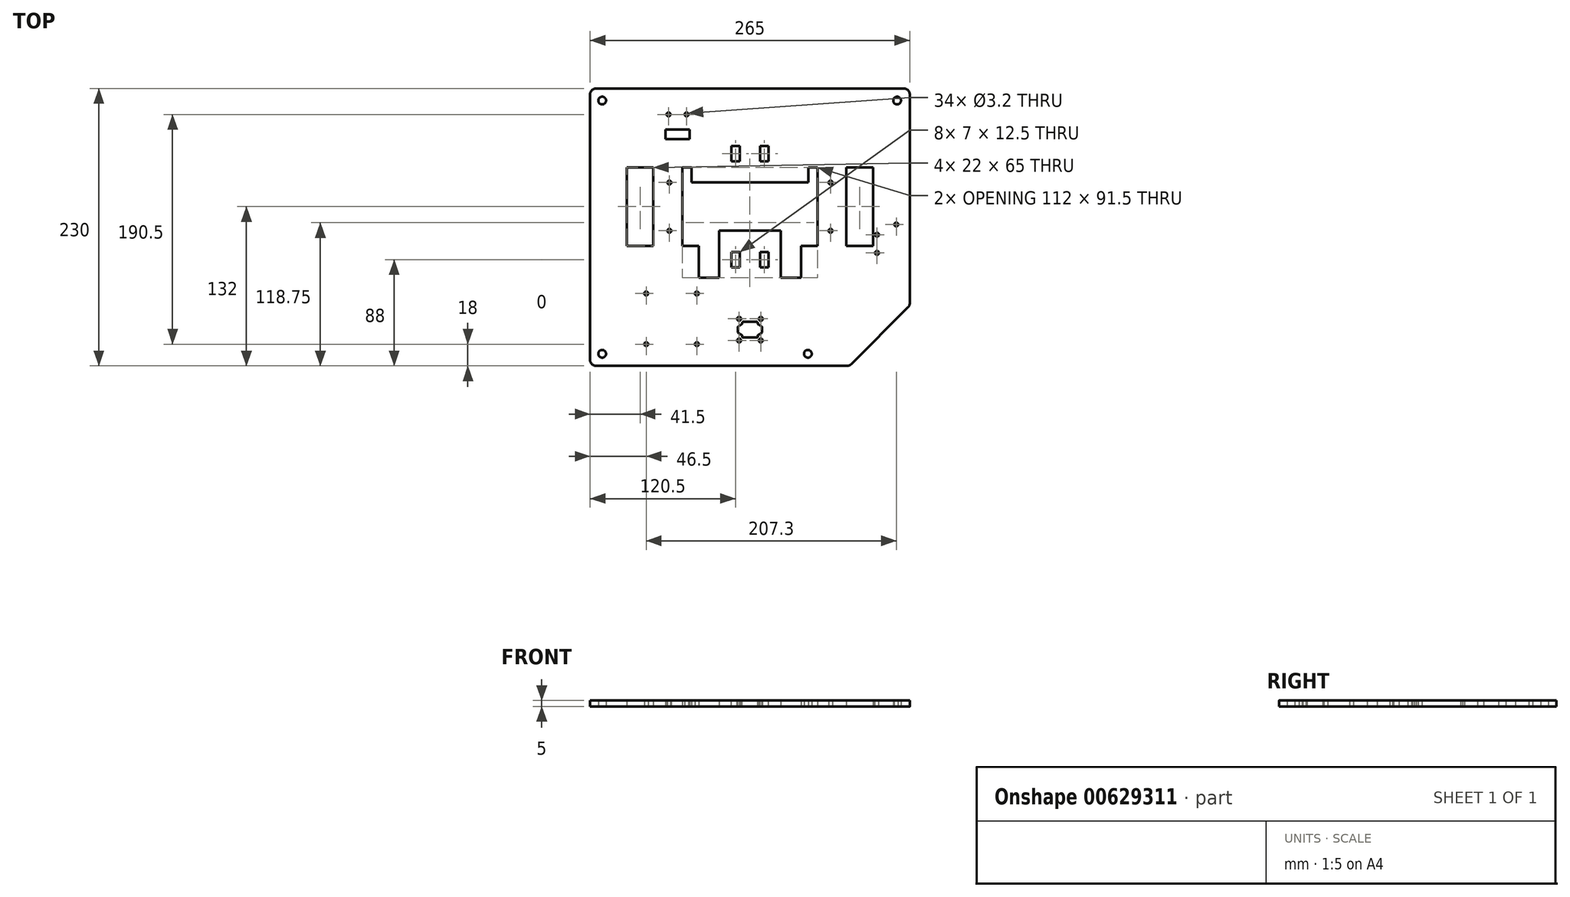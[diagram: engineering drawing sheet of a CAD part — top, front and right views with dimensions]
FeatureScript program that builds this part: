
annotation { "Feature Type Name" : "Feature", "Feature Type Description" : "" }
export const myFeature = defineFeature(function(context is Context, id is Id, definition is map)
    precondition{}
    {
        {
            var Q0;
            Q0=qCreatedBy(makeId("Top.planeOp"),FACE);
            var sketch = newSketch(context, id + "F0", { "sketchPlane" : qUnion([Q0])});
            skLineSegment(sketch, "E0.bottom", {"start": v(132.5, -132) * mm, "end": v(-132.5, -132) * mm});
            skLineSegment(sketch, "E0.top", {"start": v(132.5, 98) * mm, "end": v(-132.5, 98) * mm});
            skLineSegment(sketch, "E0.left", {"start": v(132.5, -132) * mm, "end": v(132.5, 98) * mm});
            skLineSegment(sketch, "E0.right", {"start": v(-132.5, -132) * mm, "end": v(-132.5, 98) * mm});
            skPoint(sketch, "E0.middle", {"position": v(0, -17) * mm});
            skLineSegment(sketch, "E1.bottom", {"start": v(-80, -32.5) * mm, "end": v(-102, -32.5) * mm});
            skLineSegment(sketch, "E1.top", {"start": v(-80, 32.5) * mm, "end": v(-102, 32.5) * mm});
            skLineSegment(sketch, "E1.left", {"start": v(-80, -32.5) * mm, "end": v(-80, 32.5) * mm});
            skLineSegment(sketch, "E1.right", {"start": v(-102, -32.5) * mm, "end": v(-102, 32.5) * mm});
            skPoint(sketch, "E1.middle", {"position": v(-91, 0) * mm});
            skLineSegment(sketch, "E2.bottom", {"start": v(102, -32.5) * mm, "end": v(80, -32.5) * mm});
            skLineSegment(sketch, "E2.top", {"start": v(102, 32.5) * mm, "end": v(80, 32.5) * mm});
            skLineSegment(sketch, "E2.left", {"start": v(102, -32.5) * mm, "end": v(102, 32.5) * mm});
            skLineSegment(sketch, "E2.right", {"start": v(80, -32.5) * mm, "end": v(80, 32.5) * mm});
            skPoint(sketch, "E2.middle", {"position": v(91, 0) * mm});
            skLineSegment(sketch, "E3.bottom", {"start": v(56, -32.5) * mm, "end": v(42.5, -32.5) * mm});
            skLineSegment(sketch, "E3.top", {"start": v(56, 32.5) * mm, "end": v(48.5, 32.5) * mm});
            skLineSegment(sketch, "E3.left", {"start": v(56, -32.5) * mm, "end": v(56, 32.5) * mm});
            skLineSegment(sketch, "E3.right", {"start": v(-56, -32.5) * mm, "end": v(-56, 32.5) * mm});
            skPoint(sketch, "E3.middle", {"position": v(0, 0) * mm});
            skPoint(sketch, "E3.middle.positionSnap0", {"position": v(0, 98) * mm});
            skPoint(sketch, "E3.centerSnap0", {"position": v(0, 98) * mm});
            skLineSegment(sketch, "E4.bottom", {"start": v(66.75, -20) * mm, "end": v(-66.75, -20) * mm, "construction": true});
            skLineSegment(sketch, "E4.top", {"start": v(66.75, 20) * mm, "end": v(-66.75, 20) * mm, "construction": true});
            skLineSegment(sketch, "E4.left", {"start": v(66.75, -20) * mm, "end": v(66.75, 20) * mm, "construction": true});
            skLineSegment(sketch, "E4.right", {"start": v(-66.75, -20) * mm, "end": v(-66.75, 20) * mm, "construction": true});
            skLineSegment(sketch, "E5.bottom", {"start": v(-25.5, -59) * mm, "end": v(-42.5, -59) * mm});
            skLineSegment(sketch, "E5.left", {"start": v(-25.5, -59) * mm, "end": v(-25.5, -20) * mm});
            skLineSegment(sketch, "E5.right", {"start": v(-42.5, -59) * mm, "end": v(-42.5, -32.5) * mm});
            skPoint(sketch, "E5.middle", {"position": v(-34, -45.75) * mm});
            skLineSegment(sketch, "E6.bottom", {"start": v(42.5, -59) * mm, "end": v(25.5, -59) * mm});
            skLineSegment(sketch, "E6.left", {"start": v(42.5, -59) * mm, "end": v(42.5, -32.5) * mm});
            skLineSegment(sketch, "E6.right", {"start": v(25.5, -59) * mm, "end": v(25.5, -20) * mm});
            skPoint(sketch, "E6.middle", {"position": v(34, -45.75) * mm});
            skLineSegment(sketch, "E7.trimOffspring", {"start": v(-42.5, -32.5) * mm, "end": v(-56, -32.5) * mm});
            skLineSegment(sketch, "E8.trimOffspring", {"start": v(25.5, -20) * mm, "end": v(-25.5, -20) * mm});
            skLineSegment(sketch, "E9.top", {"start": v(-48.5, 20) * mm, "end": v(48.5, 20) * mm});
            skLineSegment(sketch, "E9.left", {"start": v(-48.5, 32.5) * mm, "end": v(-48.5, 20) * mm});
            skLineSegment(sketch, "E9.right", {"start": v(48.5, 32.5) * mm, "end": v(48.5, 20) * mm});
            skLineSegment(sketch, "E10.trimOffspring", {"start": v(-48.5, 32.5) * mm, "end": v(-56, 32.5) * mm});
            skLineSegment(sketch, "E11", {"start": v(-132.5, 0) * mm, "end": v(132.5, 0) * mm, "construction": true});
            skSolve(sketch);
        }
        {
            var Q0;
            Q0=makeQuery(id+"F0.imprint","IMPRINT",FACE,{"disambiguationData":[TD([[makeQuery(id+"F0.imprint","IMPRINT",EDGE,{"derivedFrom":sQuery(id+"F0.wireOp",EDGE,"E0.bottom")}),-1.0]])]});
            extrude(context, id + "F1", {"entities" : qUnion([Q0]), "depth" : 5 * mm, "offsetDistance" : 25 * mm});
        }
        {
            var Q0;
            Q0=sQuery(id+"F0.wireOp",VERTEX,"E4.right.end");
            var Q1;
            Q1=sQuery(id+"F0.wireOp",VERTEX,"E4.right.start");
            var Q2;
            Q2=sQuery(id+"F0.wireOp",VERTEX,"E4.top.start");
            var Q3;
            Q3=sQuery(id+"F0.wireOp",VERTEX,"E4.bottom.start");
            var Q4;
            Q4=makeQuery(id+"F1.opExtrude","SWEPT_BODY",BODY,{"disambiguationData":[OSD([sQuery(id+"F0.wireOp",EDGE,"E0.bottom"),sQuery(id+"F0.wireOp",EDGE,"E0.top"),sQuery(id+"F0.wireOp",EDGE,"E0.left"),sQuery(id+"F0.wireOp",EDGE,"E0.right"),sQuery(id+"F0.wireOp",EDGE,"E1.bottom"),sQuery(id+"F0.wireOp",EDGE,"E1.top"),sQuery(id+"F0.wireOp",EDGE,"E1.left"),sQuery(id+"F0.wireOp",EDGE,"E1.right"),sQuery(id+"F0.wireOp",EDGE,"E2.bottom"),sQuery(id+"F0.wireOp",EDGE,"E2.top"),sQuery(id+"F0.wireOp",EDGE,"E2.left"),sQuery(id+"F0.wireOp",EDGE,"E2.right"),sQuery(id+"F0.wireOp",EDGE,"E3.bottom"),sQuery(id+"F0.wireOp",EDGE,"E3.top"),sQuery(id+"F0.wireOp",EDGE,"E3.left"),sQuery(id+"F0.wireOp",EDGE,"E3.right")])]});
            hole(context, id + "F2", {"style" : HoleStyle.SIMPLE, "endStyle" : HoleEndStyle.THROUGH, "oppositeDirection" : true, "holeDiameter" : 3.2 * mm, "majorDiameter" : 5 * mm, "isTappedThrough" : true, "tappedDepth" : 2.3 * mm, "tapClearance" : 3, "startFromSketch" : true, "locations" : qUnion([Q0, Q1, Q2, Q3]), "scope" : qUnion([Q4])});
        }
        {
            var Q0;
            Q0=makeQuery(id+"F1.opExtrude","SWEPT_FACE",FACE,{"disambiguationData":[OSD([sQuery(id+"F0.wireOp",EDGE,"E0.bottom")])]});
            var Q1;
            Q1=makeQuery(id+"F1.opExtrude","SWEPT_FACE",FACE,{"disambiguationData":[OSD([sQuery(id+"F0.wireOp",EDGE,"E0.top")])]});
            cPlane(context, id + "F3", {"entities" : qUnion([Q0, Q1]), "cplaneType" : CPlaneType.MID_PLANE, "offset" : 25 * mm, "width" : 150 * mm, "height" : 150 * mm});
        }
        {
            var Q0;
            Q0=makeQuery(id+"F1.opExtrude","CAP_FACE",FACE,{"disambiguationData":[OSD([sQuery(id+"F0.wireOp",EDGE,"E0.bottom"),sQuery(id+"F0.wireOp",EDGE,"E0.top"),sQuery(id+"F0.wireOp",EDGE,"E0.left"),sQuery(id+"F0.wireOp",EDGE,"E0.right"),sQuery(id+"F0.wireOp",EDGE,"E1.bottom"),sQuery(id+"F0.wireOp",EDGE,"E1.top"),sQuery(id+"F0.wireOp",EDGE,"E1.left"),sQuery(id+"F0.wireOp",EDGE,"E1.right"),sQuery(id+"F0.wireOp",EDGE,"E2.bottom"),sQuery(id+"F0.wireOp",EDGE,"E2.top"),sQuery(id+"F0.wireOp",EDGE,"E2.left"),sQuery(id+"F0.wireOp",EDGE,"E2.right"),sQuery(id+"F0.wireOp",EDGE,"E3.bottom"),sQuery(id+"F0.wireOp",EDGE,"E3.top"),sQuery(id+"F0.wireOp",EDGE,"E3.left"),sQuery(id+"F0.wireOp",EDGE,"E3.right")])],"isStart":false});
            var sketch = newSketch(context, id + "F4", { "sketchPlane" : qUnion([Q0])});
            skLineSegment(sketch, "E12", {"start": v(-6.73, -102) * mm, "end": v(6.73, -102) * mm, "construction": true});
            skLineSegment(sketch, "E13.bottom", {"start": v(6.5, -108.5) * mm, "end": v(-6.5, -108.5) * mm});
            skLineSegment(sketch, "E13.top", {"start": v(6.5, -95.5) * mm, "end": v(-6.5, -95.5) * mm});
            skLineSegment(sketch, "E13.left", {"start": v(6.5, -108.5) * mm, "end": v(6.5, -106.52) * mm});
            skLineSegment(sketch, "E13.right", {"start": v(-6.5, -108.5) * mm, "end": v(-6.5, -106.52) * mm});
            skPoint(sketch, "E13.middle", {"position": v(0, -102) * mm});
            skLineSegment(sketch, "E14.bottom", {"start": v(9, -111) * mm, "end": v(-9, -111) * mm, "construction": true});
            skLineSegment(sketch, "E14.top", {"start": v(9, -93) * mm, "end": v(-9, -93) * mm, "construction": true});
            skLineSegment(sketch, "E14.left", {"start": v(9, -111) * mm, "end": v(9, -93) * mm, "construction": true});
            skLineSegment(sketch, "E14.right", {"start": v(-9, -111) * mm, "end": v(-9, -93) * mm, "construction": true});
            skLineSegment(sketch, "E15.left", {"start": v(10, -104.5) * mm, "end": v(10, -99.5) * mm});
            skLineSegment(sketch, "E15.right", {"start": v(-10, -104.5) * mm, "end": v(-10, -99.5) * mm});
            skLineSegment(sketch, "E16.trimOffspring", {"start": v(-6.5, -97.48) * mm, "end": v(-6.5, -95.5) * mm});
            skLineSegment(sketch, "E17.trimOffspring", {"start": v(6.5, -97.48) * mm, "end": v(6.5, -95.5) * mm});
            skLineSegment(sketch, "E18", {"start": v(-10, -99.5) * mm, "end": v(-6.5, -97.48) * mm});
            skLineSegment(sketch, "E19", {"start": v(-10, -104.5) * mm, "end": v(-6.5, -106.52) * mm});
            skLineSegment(sketch, "E20", {"start": v(6.5, -97.48) * mm, "end": v(10, -99.5) * mm});
            skLineSegment(sketch, "E21", {"start": v(10, -104.5) * mm, "end": v(6.5, -106.52) * mm});
            skLineSegment(sketch, "E22", {"start": v(-132.5, -17) * mm, "end": v(132.5, -17) * mm, "construction": true});
            skSolve(sketch);
        }
        {
            var Q0;
            Q0=makeQuery(id+"F4.imprint","IMPRINT",FACE,{"disambiguationData":[TD([[makeQuery(id+"F4.imprint","IMPRINT",EDGE,{"derivedFrom":sQuery(id+"F4.wireOp",EDGE,"E13.bottom")}),-1.0]])]});
            extrude(context, id + "F5", {"entities" : qUnion([Q0]), "operationType" : NewBodyOperationType.REMOVE, "endBound" : BoundingType.UP_TO_NEXT, "oppositeDirection" : true, "depth" : 25 * mm, "offsetDistance" : 25 * mm});
        }
        {
            var Q0;
            Q0=sQuery(id+"F4.wireOp",VERTEX,"E14.top.end");
            var Q1;
            Q1=sQuery(id+"F4.wireOp",VERTEX,"E14.bottom.end");
            var Q2;
            Q2=sQuery(id+"F4.wireOp",VERTEX,"E14.left.end");
            var Q3;
            Q3=sQuery(id+"F4.wireOp",VERTEX,"E14.left.start");
            var Q4;
            Q4=makeQuery(id+"F1.opExtrude","SWEPT_BODY",BODY,{"disambiguationData":[OSD([sQuery(id+"F0.wireOp",EDGE,"E0.bottom"),sQuery(id+"F0.wireOp",EDGE,"E0.top"),sQuery(id+"F0.wireOp",EDGE,"E0.left"),sQuery(id+"F0.wireOp",EDGE,"E0.right"),sQuery(id+"F0.wireOp",EDGE,"E1.bottom"),sQuery(id+"F0.wireOp",EDGE,"E1.top"),sQuery(id+"F0.wireOp",EDGE,"E1.left"),sQuery(id+"F0.wireOp",EDGE,"E1.right"),sQuery(id+"F0.wireOp",EDGE,"E2.bottom"),sQuery(id+"F0.wireOp",EDGE,"E2.top"),sQuery(id+"F0.wireOp",EDGE,"E2.left"),sQuery(id+"F0.wireOp",EDGE,"E2.right"),sQuery(id+"F0.wireOp",EDGE,"E3.bottom"),sQuery(id+"F0.wireOp",EDGE,"E3.top"),sQuery(id+"F0.wireOp",EDGE,"E3.left"),sQuery(id+"F0.wireOp",EDGE,"E3.right")])]});
            hole(context, id + "F6", {"style" : HoleStyle.SIMPLE, "endStyle" : HoleEndStyle.THROUGH, "holeDiameter" : 3.2 * mm, "majorDiameter" : 5 * mm, "isTappedThrough" : true, "tappedDepth" : 2.3 * mm, "tapClearance" : 3, "startFromSketch" : true, "locations" : qUnion([Q0, Q1, Q2, Q3]), "scope" : qUnion([Q4])});
        }
        {
            var Q0;
            Q0=makeQuery(id+"F5.boolean.opBoolean","COPY",EDGE,{"derivedFrom":makeQuery(id+"F5.opExtrude","SWEPT_EDGE",EDGE,{"disambiguationData":[OSD([sQuery(id+"F4.wireOp",EDGE,"E15.right"),sQuery(id+"F4.wireOp",EDGE,"E18")])]})});
            var Q1;
            Q1=makeQuery(id+"F5.boolean.opBoolean","COPY",EDGE,{"derivedFrom":makeQuery(id+"F5.opExtrude","SWEPT_EDGE",EDGE,{"disambiguationData":[OSD([sQuery(id+"F4.wireOp",EDGE,"E16.trimOffspring"),sQuery(id+"F4.wireOp",EDGE,"E18")])]})});
            var Q2;
            Q2=makeQuery(id+"F5.boolean.opBoolean","COPY",EDGE,{"derivedFrom":makeQuery(id+"F5.opExtrude","SWEPT_EDGE",EDGE,{"disambiguationData":[OSD([sQuery(id+"F4.wireOp",EDGE,"E13.top"),sQuery(id+"F4.wireOp",EDGE,"E16.trimOffspring")])]})});
            var Q3;
            Q3=makeQuery(id+"F5.boolean.opBoolean","COPY",EDGE,{"derivedFrom":makeQuery(id+"F5.opExtrude","SWEPT_EDGE",EDGE,{"disambiguationData":[OSD([sQuery(id+"F4.wireOp",EDGE,"E13.top"),sQuery(id+"F4.wireOp",EDGE,"E17.trimOffspring")])]})});
            var Q4;
            Q4=makeQuery(id+"F5.boolean.opBoolean","COPY",EDGE,{"derivedFrom":makeQuery(id+"F5.opExtrude","SWEPT_EDGE",EDGE,{"disambiguationData":[OSD([sQuery(id+"F4.wireOp",EDGE,"E17.trimOffspring"),sQuery(id+"F4.wireOp",EDGE,"E20")])]})});
            var Q5;
            Q5=makeQuery(id+"F5.boolean.opBoolean","COPY",EDGE,{"derivedFrom":makeQuery(id+"F5.opExtrude","SWEPT_EDGE",EDGE,{"disambiguationData":[OSD([sQuery(id+"F4.wireOp",EDGE,"E15.left"),sQuery(id+"F4.wireOp",EDGE,"E20")])]})});
            var Q6;
            Q6=makeQuery(id+"F5.boolean.opBoolean","COPY",EDGE,{"derivedFrom":makeQuery(id+"F5.opExtrude","SWEPT_EDGE",EDGE,{"disambiguationData":[OSD([sQuery(id+"F4.wireOp",EDGE,"E15.left"),sQuery(id+"F4.wireOp",EDGE,"E21")])]})});
            var Q7;
            Q7=makeQuery(id+"F5.boolean.opBoolean","COPY",EDGE,{"derivedFrom":makeQuery(id+"F5.opExtrude","SWEPT_EDGE",EDGE,{"disambiguationData":[OSD([sQuery(id+"F4.wireOp",EDGE,"E13.left"),sQuery(id+"F4.wireOp",EDGE,"E21")])]})});
            var Q8;
            Q8=makeQuery(id+"F5.boolean.opBoolean","COPY",EDGE,{"derivedFrom":makeQuery(id+"F5.opExtrude","SWEPT_EDGE",EDGE,{"disambiguationData":[OSD([sQuery(id+"F4.wireOp",EDGE,"E13.bottom"),sQuery(id+"F4.wireOp",EDGE,"E13.left")])]})});
            var Q9;
            Q9=makeQuery(id+"F5.boolean.opBoolean","COPY",EDGE,{"derivedFrom":makeQuery(id+"F5.opExtrude","SWEPT_EDGE",EDGE,{"disambiguationData":[OSD([sQuery(id+"F4.wireOp",EDGE,"E13.bottom"),sQuery(id+"F4.wireOp",EDGE,"E13.right")])]})});
            var Q10;
            Q10=makeQuery(id+"F5.boolean.opBoolean","COPY",EDGE,{"derivedFrom":makeQuery(id+"F5.opExtrude","SWEPT_EDGE",EDGE,{"disambiguationData":[OSD([sQuery(id+"F4.wireOp",EDGE,"E13.right"),sQuery(id+"F4.wireOp",EDGE,"E19")])]})});
            var Q11;
            Q11=makeQuery(id+"F5.boolean.opBoolean","COPY",EDGE,{"derivedFrom":makeQuery(id+"F5.opExtrude","SWEPT_EDGE",EDGE,{"disambiguationData":[OSD([sQuery(id+"F4.wireOp",EDGE,"E15.right"),sQuery(id+"F4.wireOp",EDGE,"E19")])]})});
            fillet(context, id + "F7", {"entities" : qUnion([Q0, Q1, Q2, Q3, Q4, Q5, Q6, Q7, Q8, Q9, Q10, Q11]), "radius" : 1 * mm, "tangentPropagation" : true, "allowEdgeOverflow" : false});
        }
        {
            var Q0;
            Q0=makeQuery(id+"F1.opExtrude","CAP_FACE",FACE,{"disambiguationData":[OSD([sQuery(id+"F0.wireOp",EDGE,"E0.bottom"),sQuery(id+"F0.wireOp",EDGE,"E0.top"),sQuery(id+"F0.wireOp",EDGE,"E0.left"),sQuery(id+"F0.wireOp",EDGE,"E0.right"),sQuery(id+"F0.wireOp",EDGE,"E1.bottom"),sQuery(id+"F0.wireOp",EDGE,"E1.top"),sQuery(id+"F0.wireOp",EDGE,"E1.left"),sQuery(id+"F0.wireOp",EDGE,"E1.right"),sQuery(id+"F0.wireOp",EDGE,"E2.bottom"),sQuery(id+"F0.wireOp",EDGE,"E2.top"),sQuery(id+"F0.wireOp",EDGE,"E2.left"),sQuery(id+"F0.wireOp",EDGE,"E2.right"),sQuery(id+"F0.wireOp",EDGE,"E3.bottom"),sQuery(id+"F0.wireOp",EDGE,"E3.top"),sQuery(id+"F0.wireOp",EDGE,"E3.left"),sQuery(id+"F0.wireOp",EDGE,"E3.right"),sQuery(id+"F0.wireOp",EDGE,"E5.bottom"),sQuery(id+"F0.wireOp",EDGE,"E5.left"),sQuery(id+"F0.wireOp",EDGE,"E5.right"),sQuery(id+"F0.wireOp",EDGE,"E6.bottom"),sQuery(id+"F0.wireOp",EDGE,"E6.left"),sQuery(id+"F0.wireOp",EDGE,"E6.right"),sQuery(id+"F0.wireOp",EDGE,"E7.trimOffspring"),sQuery(id+"F0.wireOp",EDGE,"E8.trimOffspring"),sQuery(id+"F0.wireOp",EDGE,"E9.top"),sQuery(id+"F0.wireOp",EDGE,"E9.left"),sQuery(id+"F0.wireOp",EDGE,"E9.right"),sQuery(id+"F0.wireOp",EDGE,"E10.trimOffspring")])],"isStart":false});
            var sketch = newSketch(context, id + "F8", { "sketchPlane" : qUnion([Q0])});
            skLineSegment(sketch, "E23.bottom", {"start": v(-15.5, -37.75) * mm, "end": v(-8.5, -37.75) * mm});
            skLineSegment(sketch, "E23.top", {"start": v(-15.5, -50.25) * mm, "end": v(-8.5, -50.25) * mm});
            skLineSegment(sketch, "E23.left", {"start": v(-15.5, -37.75) * mm, "end": v(-15.5, -50.25) * mm});
            skLineSegment(sketch, "E23.right", {"start": v(-8.5, -37.75) * mm, "end": v(-8.5, -50.25) * mm});
            skLineSegment(sketch, "E24.MirrorCS", {"start": v(15.5, -37.75) * mm, "end": v(8.5, -37.75) * mm});
            skLineSegment(sketch, "E25.MirrorCS", {"start": v(15.5, -37.75) * mm, "end": v(15.5, -50.25) * mm});
            skLineSegment(sketch, "E26.MirrorCS", {"start": v(15.5, -50.25) * mm, "end": v(8.5, -50.25) * mm});
            skLineSegment(sketch, "E27.MirrorCS", {"start": v(8.5, -37.75) * mm, "end": v(8.5, -50.25) * mm});
            skLineSegment(sketch, "E28.MirrorCS", {"start": v(-15.5, 37.75) * mm, "end": v(-8.5, 37.75) * mm});
            skLineSegment(sketch, "E29.MirrorCS", {"start": v(15.5, 37.75) * mm, "end": v(8.5, 37.75) * mm});
            skLineSegment(sketch, "E30.MirrorCS", {"start": v(8.5, 37.75) * mm, "end": v(8.5, 50.25) * mm});
            skLineSegment(sketch, "E31.MirrorCS", {"start": v(15.5, 37.75) * mm, "end": v(15.5, 50.25) * mm});
            skLineSegment(sketch, "E32.MirrorCS", {"start": v(15.5, 50.25) * mm, "end": v(8.5, 50.25) * mm});
            skLineSegment(sketch, "E33.MirrorCS", {"start": v(-15.5, 50.25) * mm, "end": v(-8.5, 50.25) * mm});
            skLineSegment(sketch, "E34.MirrorCS", {"start": v(-8.5, 37.75) * mm, "end": v(-8.5, 50.25) * mm});
            skLineSegment(sketch, "E35.MirrorCS", {"start": v(-15.5, 37.75) * mm, "end": v(-15.5, 50.25) * mm});
            skPoint(sketch, "E36", {"position": v(-12, 44) * mm});
            skPoint(sketch, "E36.positionSnap0", {"position": v(-15.5, 44) * mm});
            skPoint(sketch, "E36.positionSnap1", {"position": v(-12, 50.25) * mm});
            skPoint(sketch, "E37", {"position": v(-12, -44) * mm});
            skPoint(sketch, "E37.positionSnap0", {"position": v(-15.5, -44) * mm});
            skPoint(sketch, "E37.positionSnap1", {"position": v(-12, -37.75) * mm});
            skSolve(sketch);
        }
        {
            var Q0;
            Q0=makeQuery(id+"F8.imprint","IMPRINT",FACE,{"disambiguationData":[TD([[makeQuery(id+"F8.imprint","IMPRINT",EDGE,{"derivedFrom":sQuery(id+"F8.wireOp",EDGE,"E23.bottom")}),-1.0]])]});
            var Q1;
            Q1=makeQuery(id+"F8.imprint","IMPRINT",FACE,{"disambiguationData":[TD([[makeQuery(id+"F8.imprint","IMPRINT",EDGE,{"derivedFrom":sQuery(id+"F8.wireOp",EDGE,"E24.MirrorCS")}),1.0]])]});
            var Q2;
            Q2=makeQuery(id+"F8.imprint","IMPRINT",FACE,{"disambiguationData":[TD([[makeQuery(id+"F8.imprint","IMPRINT",EDGE,{"derivedFrom":sQuery(id+"F8.wireOp",EDGE,"E28.MirrorCS")}),1.0]])]});
            var Q3;
            Q3=makeQuery(id+"F8.imprint","IMPRINT",FACE,{"disambiguationData":[TD([[makeQuery(id+"F8.imprint","IMPRINT",EDGE,{"derivedFrom":sQuery(id+"F8.wireOp",EDGE,"E29.MirrorCS")}),-1.0]])]});
            extrude(context, id + "F9", {"entities" : qUnion([Q0, Q1, Q2, Q3]), "operationType" : NewBodyOperationType.REMOVE, "endBound" : BoundingType.THROUGH_ALL, "oppositeDirection" : true, "depth" : 25 * mm, "offsetDistance" : 25 * mm});
        }
        {
            var Q0;
            Q0=makeQuery(id+"F1.opExtrude","SWEPT_EDGE",EDGE,{"disambiguationData":[OSD([sQuery(id+"F0.wireOp",EDGE,"E0.bottom"),sQuery(id+"F0.wireOp",EDGE,"E0.left")])]});
            chamfer(context, id + "F10", {"entities" : qUnion([Q0]), "chamferType" : ChamferType.TWO_OFFSETS, "width1" : 50 * mm, "oppositeDirection" : false, "width2" : 50 * mm, "tangentPropagation" : true});
        }
        {
            var Q0;
            Q0=qCreatedBy(makeId("Top.planeOp"),FACE);
            var sketch = newSketch(context, id + "F11", { "sketchPlane" : qUnion([Q0])});
            skPoint(sketch, "E38", {"position": v(-122.5, 88) * mm});
            skPoint(sketch, "E39", {"position": v(122, 88) * mm});
            skPoint(sketch, "E40", {"position": v(-122.5, -122) * mm});
            skPoint(sketch, "E41", {"position": v(48, -122) * mm});
            skLineSegment(sketch, "E42", {"start": v(-122.5, 88) * mm, "end": v(122, 88) * mm, "construction": true});
            skLineSegment(sketch, "E43", {"start": v(-122.5, 88) * mm, "end": v(-122.5, -122) * mm, "construction": true});
            skLineSegment(sketch, "E44", {"start": v(-122.5, -122) * mm, "end": v(48, -122) * mm, "construction": true});
            skSolve(sketch);
        }
        {
            var Q0;
            Q0=sQuery(id+"F11.wireOp",VERTEX,"E38");
            var Q1;
            Q1=sQuery(id+"F11.wireOp",VERTEX,"E40");
            var Q2;
            Q2=sQuery(id+"F11.wireOp",VERTEX,"E41");
            var Q3;
            Q3=sQuery(id+"F11.wireOp",VERTEX,"E39");
            var Q4;
            Q4=makeQuery(id+"F1.opExtrude","SWEPT_BODY",BODY,{"disambiguationData":[OSD([sQuery(id+"F0.wireOp",EDGE,"E0.bottom"),sQuery(id+"F0.wireOp",EDGE,"E0.top"),sQuery(id+"F0.wireOp",EDGE,"E0.left"),sQuery(id+"F0.wireOp",EDGE,"E0.right"),sQuery(id+"F0.wireOp",EDGE,"E1.bottom"),sQuery(id+"F0.wireOp",EDGE,"E1.top"),sQuery(id+"F0.wireOp",EDGE,"E1.left"),sQuery(id+"F0.wireOp",EDGE,"E1.right"),sQuery(id+"F0.wireOp",EDGE,"E2.bottom"),sQuery(id+"F0.wireOp",EDGE,"E2.top"),sQuery(id+"F0.wireOp",EDGE,"E2.left"),sQuery(id+"F0.wireOp",EDGE,"E2.right"),sQuery(id+"F0.wireOp",EDGE,"E3.bottom"),sQuery(id+"F0.wireOp",EDGE,"E3.top"),sQuery(id+"F0.wireOp",EDGE,"E3.left"),sQuery(id+"F0.wireOp",EDGE,"E3.right"),sQuery(id+"F0.wireOp",EDGE,"E5.bottom"),sQuery(id+"F0.wireOp",EDGE,"E5.left"),sQuery(id+"F0.wireOp",EDGE,"E5.right"),sQuery(id+"F0.wireOp",EDGE,"E6.bottom"),sQuery(id+"F0.wireOp",EDGE,"E6.left"),sQuery(id+"F0.wireOp",EDGE,"E6.right"),sQuery(id+"F0.wireOp",EDGE,"E7.trimOffspring"),sQuery(id+"F0.wireOp",EDGE,"E8.trimOffspring"),sQuery(id+"F0.wireOp",EDGE,"E9.top"),sQuery(id+"F0.wireOp",EDGE,"E9.left"),sQuery(id+"F0.wireOp",EDGE,"E9.right"),sQuery(id+"F0.wireOp",EDGE,"E10.trimOffspring")])]});
            hole(context, id + "F12", {"style" : HoleStyle.SIMPLE, "endStyle" : HoleEndStyle.THROUGH, "oppositeDirection" : true, "holeDiameter" : 6.4 * mm, "majorDiameter" : 5 * mm, "isTappedThrough" : true, "tappedDepth" : 2.3 * mm, "tapClearance" : 3, "startFromSketch" : true, "locations" : qUnion([Q0, Q1, Q2, Q3]), "scope" : qUnion([Q4])});
        }
        {
            var Q0;
            Q0=qCreatedBy(makeId("Top.planeOp"),FACE);
            var sketch = newSketch(context, id + "F13", { "sketchPlane" : qUnion([Q0])});
            skLineSegment(sketch, "E45.bottom", {"start": v(-44, -114) * mm, "end": v(-86, -114) * mm, "construction": true});
            skLineSegment(sketch, "E45.top", {"start": v(-44, -72) * mm, "end": v(-86, -72) * mm, "construction": true});
            skLineSegment(sketch, "E45.left", {"start": v(-44, -114) * mm, "end": v(-44, -72) * mm, "construction": true});
            skLineSegment(sketch, "E45.right", {"start": v(-86, -114) * mm, "end": v(-86, -72) * mm, "construction": true});
            skPoint(sketch, "E45.middle", {"position": v(-65, -93) * mm});
            skCircle(sketch, "E46", {"center": v(-65, -93) * mm, "radius": 38 * mm, "construction": true});
            skSolve(sketch);
        }
        {
            var Q0;
            Q0=makeQuery(id+"F1.opExtrude","SWEPT_EDGE",EDGE,{"disambiguationData":[OSD([sQuery(id+"F0.wireOp",EDGE,"E0.bottom"),sQuery(id+"F0.wireOp",EDGE,"E0.right")])]});
            var Q1;
            Q1=makeQuery(id+"F1.opExtrude","SWEPT_EDGE",EDGE,{"disambiguationData":[OSD([sQuery(id+"F0.wireOp",EDGE,"E0.top"),sQuery(id+"F0.wireOp",EDGE,"E0.right")])]});
            var Q2;
            Q2=makeQuery(id+"F1.opExtrude","SWEPT_EDGE",EDGE,{"disambiguationData":[OSD([sQuery(id+"F0.wireOp",EDGE,"E0.top"),sQuery(id+"F0.wireOp",EDGE,"E0.left")])]});
            var Q3;
            {var subQ0=sQuery(id+"F0.wireOp",EDGE,"E0.left");Q3=makeQuery(id+"F10.opChamfer","BLEND_EDGE",EDGE,{"blendedFrom":[makeQuery(id+"F1.opExtrude","SWEPT_EDGE",EDGE,{"disambiguationData":[OSD([sQuery(id+"F0.wireOp",EDGE,"E0.bottom"),subQ0])]}),makeQuery(id+"F1.opExtrude","SWEPT_FACE",FACE,{"disambiguationData":[OSD([subQ0])]})],"blendedInto":[makeQuery(id+"F1.opExtrude","SWEPT_FACE",FACE,{"disambiguationData":[OSD([subQ0])]})]});}
            var Q4;
            {var subQ0=sQuery(id+"F0.wireOp",EDGE,"E0.bottom");Q4=makeQuery(id+"F10.opChamfer","BLEND_EDGE",EDGE,{"blendedFrom":[makeQuery(id+"F1.opExtrude","SWEPT_EDGE",EDGE,{"disambiguationData":[OSD([subQ0,sQuery(id+"F0.wireOp",EDGE,"E0.left")])]}),makeQuery(id+"F1.opExtrude","SWEPT_FACE",FACE,{"disambiguationData":[OSD([subQ0])]})],"blendedInto":[makeQuery(id+"F1.opExtrude","SWEPT_FACE",FACE,{"disambiguationData":[OSD([subQ0])]})]});}
            fillet(context, id + "F14", {"entities" : qUnion([Q0, Q1, Q2, Q3, Q4]), "radius" : 5 * mm, "tangentPropagation" : true, "allowEdgeOverflow" : false});
        }
        {
            var Q0;
            Q0=makeQuery(id+"F1.opExtrude","CAP_FACE",FACE,{"disambiguationData":[OSD([sQuery(id+"F0.wireOp",EDGE,"E0.bottom"),sQuery(id+"F0.wireOp",EDGE,"E0.top"),sQuery(id+"F0.wireOp",EDGE,"E0.left"),sQuery(id+"F0.wireOp",EDGE,"E0.right"),sQuery(id+"F0.wireOp",EDGE,"E1.bottom"),sQuery(id+"F0.wireOp",EDGE,"E1.top"),sQuery(id+"F0.wireOp",EDGE,"E1.left"),sQuery(id+"F0.wireOp",EDGE,"E1.right"),sQuery(id+"F0.wireOp",EDGE,"E2.bottom"),sQuery(id+"F0.wireOp",EDGE,"E2.top"),sQuery(id+"F0.wireOp",EDGE,"E2.left"),sQuery(id+"F0.wireOp",EDGE,"E2.right"),sQuery(id+"F0.wireOp",EDGE,"E3.bottom"),sQuery(id+"F0.wireOp",EDGE,"E3.top"),sQuery(id+"F0.wireOp",EDGE,"E3.left"),sQuery(id+"F0.wireOp",EDGE,"E3.right"),sQuery(id+"F0.wireOp",EDGE,"E5.bottom"),sQuery(id+"F0.wireOp",EDGE,"E5.left"),sQuery(id+"F0.wireOp",EDGE,"E5.right"),sQuery(id+"F0.wireOp",EDGE,"E6.bottom"),sQuery(id+"F0.wireOp",EDGE,"E6.left"),sQuery(id+"F0.wireOp",EDGE,"E6.right"),sQuery(id+"F0.wireOp",EDGE,"E7.trimOffspring"),sQuery(id+"F0.wireOp",EDGE,"E8.trimOffspring"),sQuery(id+"F0.wireOp",EDGE,"E9.top"),sQuery(id+"F0.wireOp",EDGE,"E9.left"),sQuery(id+"F0.wireOp",EDGE,"E9.right"),sQuery(id+"F0.wireOp",EDGE,"E10.trimOffspring")])],"isStart":false});
            var sketch = newSketch(context, id + "F15", { "sketchPlane" : qUnion([Q0])});
            skPoint(sketch, "E47", {"position": v(105.3, -23.3) * mm});
            skPoint(sketch, "E48", {"position": v(105.3, -38.3) * mm});
            skPoint(sketch, "E49", {"position": v(121.3, -14.8) * mm});
            skSolve(sketch);
        }
        {
            var Q0;
            Q0=sQuery(id+"F15.wireOp",VERTEX,"E47");
            var Q1;
            Q1=sQuery(id+"F15.wireOp",VERTEX,"E48");
            var Q2;
            Q2=sQuery(id+"F15.wireOp",VERTEX,"E49");
            var Q3;
            Q3=makeQuery(id+"F1.opExtrude","SWEPT_BODY",BODY,{"disambiguationData":[OSD([sQuery(id+"F0.wireOp",EDGE,"E0.bottom"),sQuery(id+"F0.wireOp",EDGE,"E0.top"),sQuery(id+"F0.wireOp",EDGE,"E0.left"),sQuery(id+"F0.wireOp",EDGE,"E0.right"),sQuery(id+"F0.wireOp",EDGE,"E1.bottom"),sQuery(id+"F0.wireOp",EDGE,"E1.top"),sQuery(id+"F0.wireOp",EDGE,"E1.left"),sQuery(id+"F0.wireOp",EDGE,"E1.right"),sQuery(id+"F0.wireOp",EDGE,"E2.bottom"),sQuery(id+"F0.wireOp",EDGE,"E2.top"),sQuery(id+"F0.wireOp",EDGE,"E2.left"),sQuery(id+"F0.wireOp",EDGE,"E2.right"),sQuery(id+"F0.wireOp",EDGE,"E3.bottom"),sQuery(id+"F0.wireOp",EDGE,"E3.top"),sQuery(id+"F0.wireOp",EDGE,"E3.left"),sQuery(id+"F0.wireOp",EDGE,"E3.right"),sQuery(id+"F0.wireOp",EDGE,"E5.bottom"),sQuery(id+"F0.wireOp",EDGE,"E5.left"),sQuery(id+"F0.wireOp",EDGE,"E5.right"),sQuery(id+"F0.wireOp",EDGE,"E6.bottom"),sQuery(id+"F0.wireOp",EDGE,"E6.left"),sQuery(id+"F0.wireOp",EDGE,"E6.right"),sQuery(id+"F0.wireOp",EDGE,"E7.trimOffspring"),sQuery(id+"F0.wireOp",EDGE,"E8.trimOffspring"),sQuery(id+"F0.wireOp",EDGE,"E9.top"),sQuery(id+"F0.wireOp",EDGE,"E9.left"),sQuery(id+"F0.wireOp",EDGE,"E9.right"),sQuery(id+"F0.wireOp",EDGE,"E10.trimOffspring")])]});
            hole(context, id + "F16", {"style" : HoleStyle.SIMPLE, "endStyle" : HoleEndStyle.BLIND, "holeDiameter" : 3.2 * mm, "majorDiameter" : 5 * mm, "holeDepth" : 5 * mm, "isTappedThrough" : true, "tappedDepth" : 2.3 * mm, "tapClearance" : 3, "startFromSketch" : true, "locations" : qUnion([Q0, Q1, Q2]), "scope" : qUnion([Q3])});
        }
        {
            var Q0;
            Q0=sQuery(id+"F13.wireOp",VERTEX,"E45.top.end");
            var Q1;
            Q1=sQuery(id+"F13.wireOp",VERTEX,"E45.bottom.end");
            var Q2;
            Q2=sQuery(id+"F13.wireOp",VERTEX,"E45.top.start");
            var Q3;
            Q3=sQuery(id+"F13.wireOp",VERTEX,"E45.bottom.start");
            var Q4;
            Q4=makeQuery(id+"F1.opExtrude","SWEPT_BODY",BODY,{"disambiguationData":[OSD([sQuery(id+"F0.wireOp",EDGE,"E0.bottom"),sQuery(id+"F0.wireOp",EDGE,"E0.top"),sQuery(id+"F0.wireOp",EDGE,"E0.left"),sQuery(id+"F0.wireOp",EDGE,"E0.right"),sQuery(id+"F0.wireOp",EDGE,"E1.bottom"),sQuery(id+"F0.wireOp",EDGE,"E1.top"),sQuery(id+"F0.wireOp",EDGE,"E1.left"),sQuery(id+"F0.wireOp",EDGE,"E1.right"),sQuery(id+"F0.wireOp",EDGE,"E2.bottom"),sQuery(id+"F0.wireOp",EDGE,"E2.top"),sQuery(id+"F0.wireOp",EDGE,"E2.left"),sQuery(id+"F0.wireOp",EDGE,"E2.right"),sQuery(id+"F0.wireOp",EDGE,"E3.bottom"),sQuery(id+"F0.wireOp",EDGE,"E3.top"),sQuery(id+"F0.wireOp",EDGE,"E3.left"),sQuery(id+"F0.wireOp",EDGE,"E3.right"),sQuery(id+"F0.wireOp",EDGE,"E5.bottom"),sQuery(id+"F0.wireOp",EDGE,"E5.left"),sQuery(id+"F0.wireOp",EDGE,"E5.right"),sQuery(id+"F0.wireOp",EDGE,"E6.bottom"),sQuery(id+"F0.wireOp",EDGE,"E6.left"),sQuery(id+"F0.wireOp",EDGE,"E6.right"),sQuery(id+"F0.wireOp",EDGE,"E7.trimOffspring"),sQuery(id+"F0.wireOp",EDGE,"E8.trimOffspring"),sQuery(id+"F0.wireOp",EDGE,"E9.top"),sQuery(id+"F0.wireOp",EDGE,"E9.left"),sQuery(id+"F0.wireOp",EDGE,"E9.right"),sQuery(id+"F0.wireOp",EDGE,"E10.trimOffspring")])]});
            hole(context, id + "F17", {"style" : HoleStyle.SIMPLE, "endStyle" : HoleEndStyle.BLIND, "oppositeDirection" : true, "holeDiameter" : 3.2 * mm, "majorDiameter" : 5 * mm, "holeDepth" : 5 * mm, "isTappedThrough" : true, "tappedDepth" : 2.3 * mm, "tapClearance" : 3, "startFromSketch" : true, "locations" : qUnion([Q0, Q1, Q2, Q3]), "scope" : qUnion([Q4])});
        }
        {
            var Q0;
            Q0=qCreatedBy(makeId("Top.planeOp"),FACE);
            var sketch = newSketch(context, id + "F18", { "sketchPlane" : qUnion([Q0])});
            skCircle(sketch, "E50", {"center": v(-67.5, 76.5) * mm, "radius": 1.6 * mm});
            skCircle(sketch, "E51", {"center": v(-52.5, 76.5) * mm, "radius": 1.6 * mm});
            skLineSegment(sketch, "E52", {"start": v(-67.5, 76.5) * mm, "end": v(-52.5, 76.5) * mm, "construction": true});
            skLineSegment(sketch, "E53.bottom", {"start": v(-50, 56) * mm, "end": v(-70, 56) * mm});
            skLineSegment(sketch, "E53.top", {"start": v(-50, 64) * mm, "end": v(-70, 64) * mm});
            skLineSegment(sketch, "E53.left", {"start": v(-50, 56) * mm, "end": v(-50, 64) * mm});
            skLineSegment(sketch, "E53.right", {"start": v(-70, 56) * mm, "end": v(-70, 64) * mm});
            skPoint(sketch, "E53.middle", {"position": v(-60, 60) * mm});
            skLineSegment(sketch, "E54", {"start": v(-76.5, 60) * mm, "end": v(-40.5, 60) * mm, "construction": true});
            skSolve(sketch);
        }
        {
            var Q0;
            Q0 = qSketchRegion(id + "F18", true);
            extrude(context, id + "F19", {"entities" : qUnion([Q0]), "operationType" : NewBodyOperationType.REMOVE, "depth" : 25 * mm, "offsetDistance" : 25 * mm});
        }
    });
